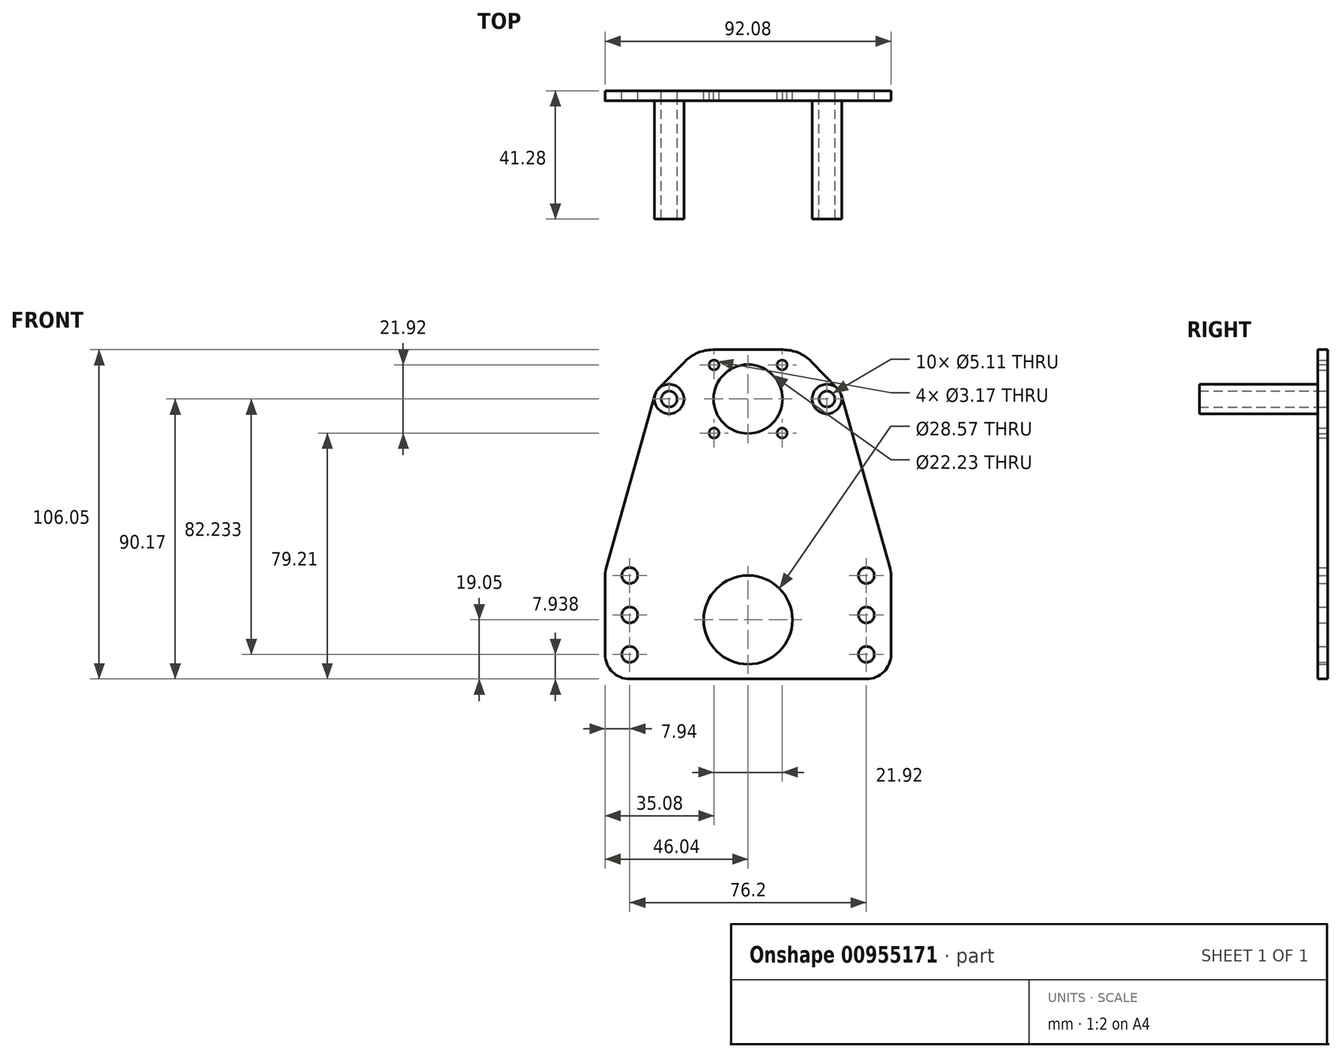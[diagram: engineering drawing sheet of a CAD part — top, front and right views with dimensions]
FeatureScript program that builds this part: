
annotation { "Feature Type Name" : "Feature", "Feature Type Description" : "" }
export const myFeature = defineFeature(function(context is Context, id is Id, definition is map)
    precondition{}
    {
        {
            var Q0;
            Q0=qCreatedBy(makeId("Front.planeOp"),FACE);
            var sketch = newSketch(context, id + "F0", { "sketchPlane" : qUnion([Q0])});
            skLineSegment(sketch, "E0", {"start": v(-25.4, 0) * mm, "end": v(0, 0) * mm, "construction": true});
            skLineSegment(sketch, "E1", {"start": v(25.4, 0) * mm, "end": v(0, 0) * mm, "construction": true});
            skCircle(sketch, "E2", {"center": v(-25.4, 0) * mm, "radius": 2.55 * mm});
            skCircle(sketch, "E3", {"center": v(25.4, 0) * mm, "radius": 2.55 * mm});
            skLineSegment(sketch, "E4.bottom", {"start": v(16.67, 15.88) * mm, "end": v(-16.67, 15.88) * mm, "construction": true});
            skLineSegment(sketch, "E4.top", {"start": v(16.67, -15.88) * mm, "end": v(-16.67, -15.88) * mm, "construction": true});
            skLineSegment(sketch, "E4.left", {"start": v(16.67, 15.88) * mm, "end": v(16.67, -15.88) * mm, "construction": true});
            skLineSegment(sketch, "E4.right", {"start": v(-16.67, 15.88) * mm, "end": v(-16.67, -15.88) * mm, "construction": true});
            skPoint(sketch, "E4.middle", {"position": v(0, 0) * mm});
            skLineSegment(sketch, "E5.bottom", {"start": v(10.96, 10.96) * mm, "end": v(-10.96, 10.96) * mm, "construction": true});
            skLineSegment(sketch, "E5.top", {"start": v(10.96, -10.96) * mm, "end": v(-10.96, -10.96) * mm, "construction": true});
            skLineSegment(sketch, "E5.left", {"start": v(10.96, 10.96) * mm, "end": v(10.96, -10.96) * mm, "construction": true});
            skLineSegment(sketch, "E5.right", {"start": v(-10.96, 10.96) * mm, "end": v(-10.96, -10.96) * mm, "construction": true});
            skCircle(sketch, "E6", {"center": v(10.96, 10.96) * mm, "radius": 1.59 * mm});
            skCircle(sketch, "E7", {"center": v(10.96, -10.96) * mm, "radius": 1.59 * mm});
            skCircle(sketch, "E8", {"center": v(-10.96, -10.96) * mm, "radius": 1.59 * mm});
            skCircle(sketch, "E9", {"center": v(-10.96, 10.96) * mm, "radius": 1.59 * mm});
            skArc(sketch, "E10", {"start": v(-28.82, 3.31) * mm, "mid": v(-30.16, 0) * mm, "end": v(-28.82, -3.31) * mm, "construction": true});
            skArc(sketch, "E11", {"start": v(28.82, 3.31) * mm, "mid": v(30.16, 0) * mm, "end": v(28.82, -3.31) * mm, "construction": true});
            skLineSegment(sketch, "E12", {"start": v(-28.82, 3.31) * mm, "end": v(-20.41, 12) * mm});
            skLineSegment(sketch, "E13", {"start": v(-28.82, -3.31) * mm, "end": v(-20.41, -12) * mm, "construction": true});
            skLineSegment(sketch, "E14", {"start": v(28.82, 3.31) * mm, "end": v(20.41, 12) * mm});
            skLineSegment(sketch, "E15", {"start": v(28.82, -3.31) * mm, "end": v(20.41, -12) * mm, "construction": true});
            skCircle(sketch, "E16", {"center": v(25.4, 0) * mm, "radius": 4.76 * mm, "construction": true});
            skCircle(sketch, "E17", {"center": v(-25.4, 0) * mm, "radius": 4.76 * mm, "construction": true});
            skLineSegment(sketch, "E18", {"start": v(-11.28, 15.88) * mm, "end": v(11.28, 15.88) * mm});
            skLineSegment(sketch, "E19", {"start": v(11.28, -15.88) * mm, "end": v(-11.28, -15.88) * mm, "construction": true});
            skPoint(sketch, "E20.visualSharp", {"position": v(-16.67, 15.88) * mm});
            skArc(sketch, "E20.filletArc", {"start": v(-11.28, 15.88) * mm, "mid": v(-16.24, 14.87) * mm, "end": v(-20.41, 12) * mm});
            skPoint(sketch, "E21.visualSharp", {"position": v(16.67, 15.88) * mm});
            skArc(sketch, "E21.filletArc", {"start": v(20.41, 12) * mm, "mid": v(16.24, 14.87) * mm, "end": v(11.28, 15.88) * mm});
            skPoint(sketch, "E22.visualSharp", {"position": v(16.67, -15.88) * mm});
            skArc(sketch, "E22.filletArc", {"start": v(11.28, -15.88) * mm, "mid": v(16.24, -14.87) * mm, "end": v(20.41, -12) * mm, "construction": true});
            skPoint(sketch, "E23.visualSharp", {"position": v(-16.67, -15.88) * mm});
            skArc(sketch, "E23.filletArc", {"start": v(-20.41, -12) * mm, "mid": v(-16.24, -14.87) * mm, "end": v(-11.28, -15.88) * mm, "construction": true});
            skCircle(sketch, "E24", {"center": v(0, 0) * mm, "radius": 11.11 * mm});
            skCircle(sketch, "E25", {"center": v(0, -71.12) * mm, "radius": 14.29 * mm});
            skLineSegment(sketch, "E26.bottom", {"start": v(38.1, -56.83) * mm, "end": v(-38.1, -56.83) * mm, "construction": true});
            skLineSegment(sketch, "E26.top", {"start": v(38.1, -82.23) * mm, "end": v(-38.1, -82.23) * mm, "construction": true});
            skLineSegment(sketch, "E26.left", {"start": v(38.1, -56.83) * mm, "end": v(38.1, -82.23) * mm, "construction": true});
            skLineSegment(sketch, "E26.right", {"start": v(-38.1, -56.83) * mm, "end": v(-38.1, -82.23) * mm, "construction": true});
            skPoint(sketch, "E26.middle", {"position": v(0, -69.53) * mm});
            skCircle(sketch, "E27", {"center": v(38.1, -56.83) * mm, "radius": 2.55 * mm});
            skCircle(sketch, "E28", {"center": v(-38.1, -56.83) * mm, "radius": 2.55 * mm});
            skCircle(sketch, "E29", {"center": v(38.1, -82.23) * mm, "radius": 2.55 * mm});
            skCircle(sketch, "E30", {"center": v(-38.1, -82.23) * mm, "radius": 2.55 * mm});
            skCircle(sketch, "E31", {"center": v(38.1, -69.53) * mm, "radius": 2.55 * mm});
            skCircle(sketch, "E32", {"center": v(-38.1, -69.53) * mm, "radius": 2.55 * mm});
            skCircle(sketch, "E33", {"center": v(38.1, -56.83) * mm, "radius": 7.94 * mm, "construction": true});
            skCircle(sketch, "E34", {"center": v(-38.1, -56.83) * mm, "radius": 7.94 * mm, "construction": true});
            skCircle(sketch, "E35", {"center": v(38.1, -82.23) * mm, "radius": 7.94 * mm, "construction": true});
            skCircle(sketch, "E36", {"center": v(-38.1, -82.23) * mm, "radius": 7.94 * mm, "construction": true});
            skArc(sketch, "E37", {"start": v(28.82, 3.31) * mm, "mid": v(29.53, 2.37) * mm, "end": v(29.98, 1.3) * mm});
            skLineSegment(sketch, "E38", {"start": v(29.98, 1.3) * mm, "end": v(45.74, -54.68) * mm});
            skArc(sketch, "E39", {"start": v(45.74, -54.68) * mm, "mid": v(45.96, -55.75) * mm, "end": v(46.04, -56.83) * mm});
            skLineSegment(sketch, "E40", {"start": v(46.04, -56.83) * mm, "end": v(46.04, -82.23) * mm});
            skArc(sketch, "E41", {"start": v(46.04, -82.23) * mm, "mid": v(43.71, -87.85) * mm, "end": v(38.1, -90.17) * mm});
            skLineSegment(sketch, "E42", {"start": v(38.1, -90.17) * mm, "end": v(-38.1, -90.17) * mm});
            skArc(sketch, "E43", {"start": v(-38.1, -90.17) * mm, "mid": v(-43.71, -87.85) * mm, "end": v(-46.04, -82.23) * mm});
            skLineSegment(sketch, "E44", {"start": v(-46.04, -82.23) * mm, "end": v(-46.04, -56.83) * mm});
            skArc(sketch, "E45", {"start": v(-46.04, -56.83) * mm, "mid": v(-45.96, -55.75) * mm, "end": v(-45.74, -54.68) * mm});
            skLineSegment(sketch, "E46", {"start": v(-45.74, -54.68) * mm, "end": v(-29.98, 1.3) * mm});
            skArc(sketch, "E47", {"start": v(-29.98, 1.3) * mm, "mid": v(-29.53, 2.37) * mm, "end": v(-28.82, 3.31) * mm});
            skSolve(sketch);
        }
        {
            var Q0;
            Q0=makeQuery(id+"F0.imprint","IMPRINT",FACE,{"disambiguationData":[TD([[makeQuery(id+"F0.imprint","IMPRINT",EDGE,{"derivedFrom":sQuery(id+"F0.wireOp",EDGE,"E2")}),-1.0]])]});
            extrude(context, id + "F1", {"entities" : qUnion([Q0]), "depth" : 3.17 * mm, "offsetDistance" : 25.4 * mm});
        }
        {
            var Q0;
            Q0=makeQuery(id+"F1.opExtrude","CAP_FACE",FACE,{"disambiguationData":[OSD([sQuery(id+"F0.wireOp",EDGE,"E2"),sQuery(id+"F0.wireOp",EDGE,"E3"),sQuery(id+"F0.wireOp",EDGE,"E6"),sQuery(id+"F0.wireOp",EDGE,"E7"),sQuery(id+"F0.wireOp",EDGE,"E8"),sQuery(id+"F0.wireOp",EDGE,"E9"),sQuery(id+"F0.wireOp",EDGE,"E10"),sQuery(id+"F0.wireOp",EDGE,"E11"),sQuery(id+"F0.wireOp",EDGE,"E12"),sQuery(id+"F0.wireOp",EDGE,"E13"),sQuery(id+"F0.wireOp",EDGE,"E14"),sQuery(id+"F0.wireOp",EDGE,"E15"),sQuery(id+"F0.wireOp",EDGE,"E18"),sQuery(id+"F0.wireOp",EDGE,"E19"),sQuery(id+"F0.wireOp",EDGE,"E20.filletArc"),sQuery(id+"F0.wireOp",EDGE,"E21.filletArc"),sQuery(id+"F0.wireOp",EDGE,"E22.filletArc"),sQuery(id+"F0.wireOp",EDGE,"E23.filletArc"),sQuery(id+"F0.wireOp",EDGE,"E24")])],"isStart":false});
            var sketch = newSketch(context, id + "F2", { "sketchPlane" : qUnion([Q0])});
            skCircle(sketch, "E48", {"center": v(-25.4, 0) * mm, "radius": 4.76 * mm});
            skCircle(sketch, "E49", {"center": v(25.4, 0) * mm, "radius": 4.76 * mm});
            skCircle(sketch, "E50", {"center": v(-25.4, 0) * mm, "radius": 2.55 * mm});
            skCircle(sketch, "E51", {"center": v(25.4, 0) * mm, "radius": 2.55 * mm});
            skSolve(sketch);
        }
        {
            var Q0;
            Q0=qSketchRegion(id+"F2",true);
            extrude(context, id + "F3", {"entities" : qUnion([Q0]), "depth" : 38.1 * mm, "offsetDistance" : 25.4 * mm});
        }
    });
